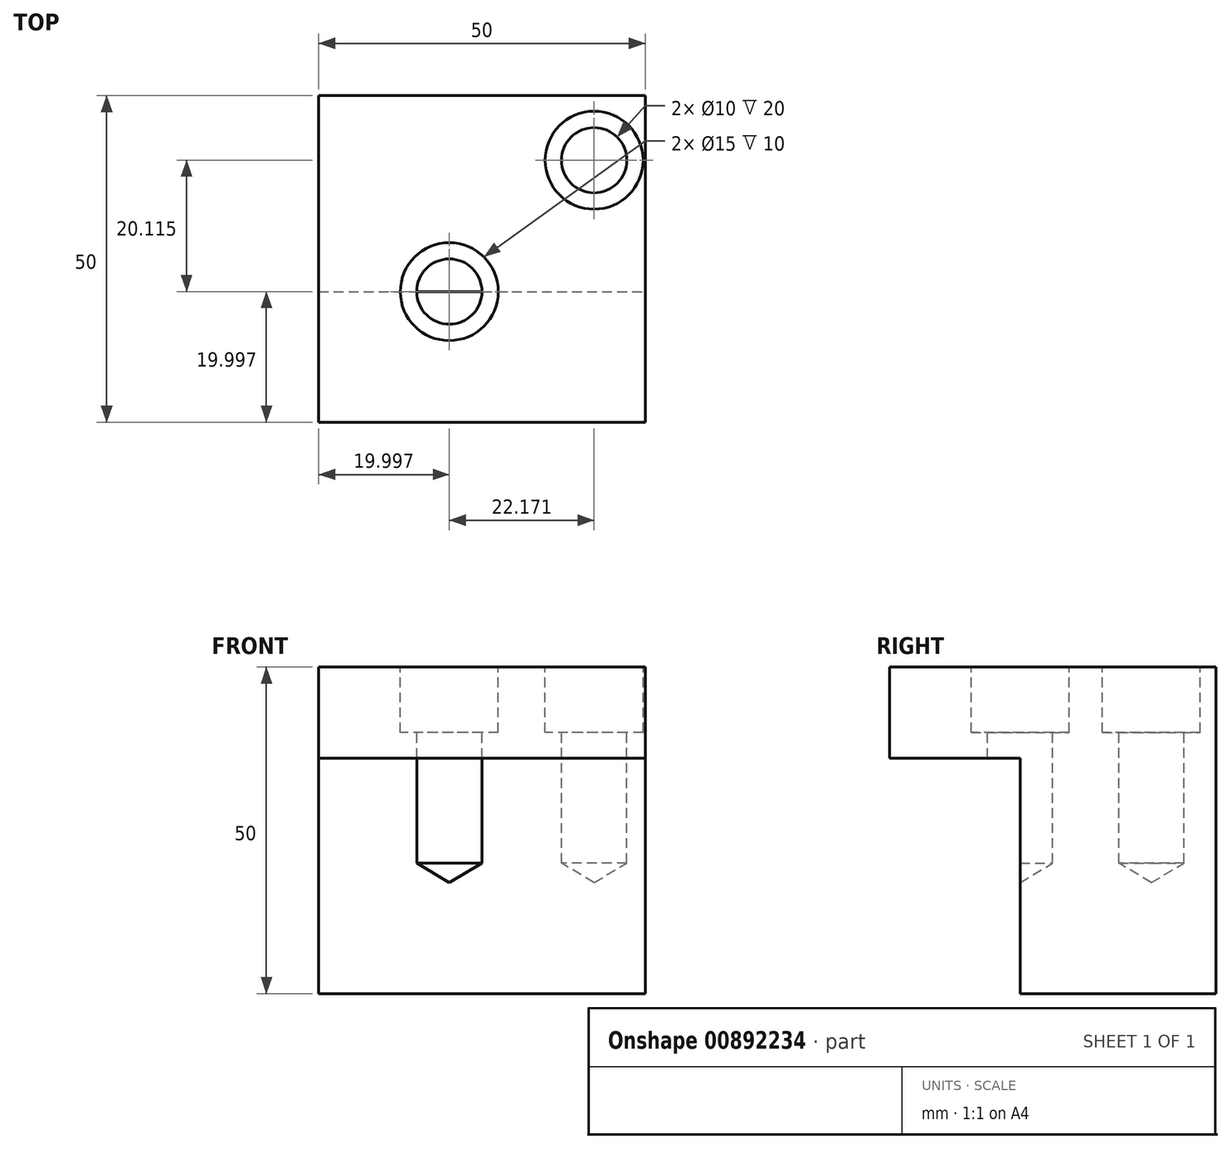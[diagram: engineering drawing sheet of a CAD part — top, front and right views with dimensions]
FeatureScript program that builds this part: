
annotation { "Feature Type Name" : "Feature", "Feature Type Description" : "" }
export const myFeature = defineFeature(function(context is Context, id is Id, definition is map)
    precondition{}
    {
        {
            var Q0;
            Q0=qCreatedBy(makeId("Top.planeOp"),FACE);
            var sketch = newSketch(context, id + "F0", { "sketchPlane" : qUnion([Q0])});
            skLineSegment(sketch, "E0.bottom", {"start": v(-51.98, -22.26) * mm, "end": v(-1.98, -22.26) * mm});
            skLineSegment(sketch, "E0.top", {"start": v(-51.98, 27.74) * mm, "end": v(-1.98, 27.74) * mm});
            skLineSegment(sketch, "E0.left", {"start": v(-51.98, -22.26) * mm, "end": v(-51.98, 27.74) * mm});
            skLineSegment(sketch, "E0.right", {"start": v(-1.98, -22.26) * mm, "end": v(-1.98, 27.74) * mm});
            skSolve(sketch);
        }
        {
            var Q0;
            Q0 = qSketchRegion(id + "F0", true);
            extrude(context, id + "F1", {"entities" : qUnion([Q0]), "depth" : 50 * mm, "offsetDistance" : 25 * mm});
        }
        {
            var Q0;
            Q0=makeQuery(id+"F1.opExtrude","CAP_FACE",FACE,{"disambiguationData":[OSD([sQuery(id+"F0.wireOp",EDGE,"E0.bottom"),sQuery(id+"F0.wireOp",EDGE,"E0.top"),sQuery(id+"F0.wireOp",EDGE,"E0.left"),sQuery(id+"F0.wireOp",EDGE,"E0.right")])],"isStart":false});
            var sketch = newSketch(context, id + "F2", { "sketchPlane" : qUnion([Q0])});
            skPoint(sketch, "E1", {"position": v(-45.06, 18.93) * mm});
            skPoint(sketch, "E2", {"position": v(-9.81, 17.85) * mm});
            skPoint(sketch, "E3", {"position": v(-31.98, -2.26) * mm});
            skSolve(sketch);
        }
        {
            var Q0;
            Q0=sQuery(id+"F2.wireOp",VERTEX,"E3");
            var Q1;
            Q1=makeQuery(id+"F1.opExtrude","SWEPT_BODY",BODY,{"disambiguationData":[OSD([sQuery(id+"F0.wireOp",EDGE,"E0.bottom"),sQuery(id+"F0.wireOp",EDGE,"E0.top"),sQuery(id+"F0.wireOp",EDGE,"E0.left"),sQuery(id+"F0.wireOp",EDGE,"E0.right")])]});
            hole(context, id + "F3", {"style" : HoleStyle.C_BORE, "endStyle" : HoleEndStyle.BLIND, "holeDiameter" : 10 * mm, "cBoreDiameter" : 15 * mm, "cBoreDepth" : 10 * mm, "majorDiameter" : 5 * mm, "holeDepth" : 30 * mm, "isTappedThrough" : true, "tappedDepth" : 12 * mm, "tapClearance" : 3, "locations" : qUnion([Q0]), "scope" : qUnion([Q1])});
        }
        {
            var Q0;
            Q0=sQuery(id+"F2.wireOp",VERTEX,"E2");
            var Q1;
            Q1=makeQuery(id+"F1.opExtrude","SWEPT_BODY",BODY,{"disambiguationData":[OSD([sQuery(id+"F0.wireOp",EDGE,"E0.bottom"),sQuery(id+"F0.wireOp",EDGE,"E0.top"),sQuery(id+"F0.wireOp",EDGE,"E0.left"),sQuery(id+"F0.wireOp",EDGE,"E0.right")])]});
            hole(context, id + "F4", {"style" : HoleStyle.C_BORE, "endStyle" : HoleEndStyle.BLIND, "holeDiameter" : 10 * mm, "cBoreDiameter" : 15 * mm, "cBoreDepth" : 10 * mm, "majorDiameter" : 5 * mm, "holeDepth" : 30 * mm, "isTappedThrough" : true, "tappedDepth" : 12 * mm, "tapClearance" : 3, "locations" : qUnion([Q0]), "scope" : qUnion([Q1])});
        }
        {
            var Q0;
            Q0=makeQuery(id+"F1.opExtrude","SWEPT_FACE",FACE,{"disambiguationData":[OSD([sQuery(id+"F0.wireOp",EDGE,"E0.bottom")])]});
            var sketch = newSketch(context, id + "F5", { "sketchPlane" : qUnion([Q0])});
            skLineSegment(sketch, "E4.bottom", {"start": v(-54.03, 36.07) * mm, "end": v(8.93, 36.07) * mm});
            skLineSegment(sketch, "E4.top", {"start": v(-54.03, -10.82) * mm, "end": v(8.93, -10.82) * mm});
            skLineSegment(sketch, "E4.left", {"start": v(-54.03, 36.07) * mm, "end": v(-54.03, -10.82) * mm});
            skLineSegment(sketch, "E4.right", {"start": v(8.93, 36.07) * mm, "end": v(8.93, -10.82) * mm});
            skSolve(sketch);
        }
        {
            var Q0;
            Q0 = qSketchRegion(id + "F5", true);
            extrude(context, id + "F6", {"entities" : qUnion([Q0]), "operationType" : NewBodyOperationType.REMOVE, "oppositeDirection" : true, "depth" : 20 * mm, "offsetDistance" : 25 * mm});
        }
    });
